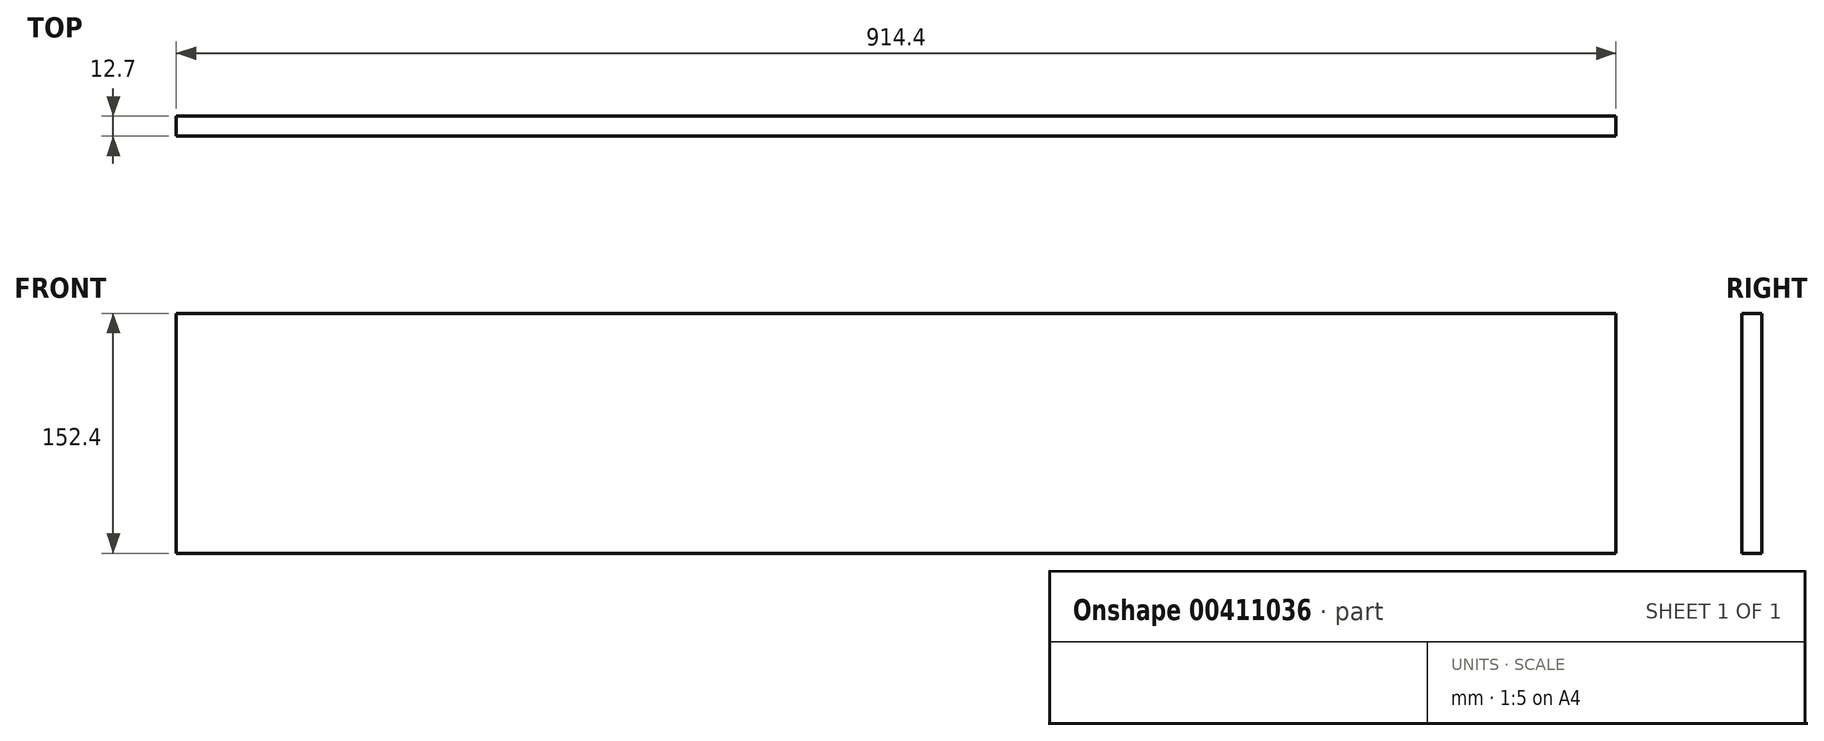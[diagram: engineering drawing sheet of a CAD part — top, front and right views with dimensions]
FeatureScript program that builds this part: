
annotation { "Feature Type Name" : "Feature", "Feature Type Description" : "" }
export const myFeature = defineFeature(function(context is Context, id is Id, definition is map)
    precondition{}
    {
        {
            var Q0;
            Q0=qCreatedBy(makeId("Front.planeOp"),FACE);
            var sketch = newSketch(context, id + "F0", { "sketchPlane" : qUnion([Q0])});
            skLineSegment(sketch, "E0.bottom", {"start": v(914.4, 0) * mm, "end": v(0, 0) * mm});
            skLineSegment(sketch, "E0.top", {"start": v(914.4, 152.4) * mm, "end": v(0, 152.4) * mm});
            skLineSegment(sketch, "E0.left", {"start": v(914.4, 0) * mm, "end": v(914.4, 152.4) * mm});
            skLineSegment(sketch, "E0.right", {"start": v(0, 0) * mm, "end": v(0, 152.4) * mm});
            skSolve(sketch);
        }
        {
            var Q0;
            Q0 = qSketchRegion(id + "F0", true);
            extrude(context, id + "F1", {"entities" : qUnion([Q0]), "oppositeDirection" : true, "depth" : 12.7 * mm});
        }
    });
